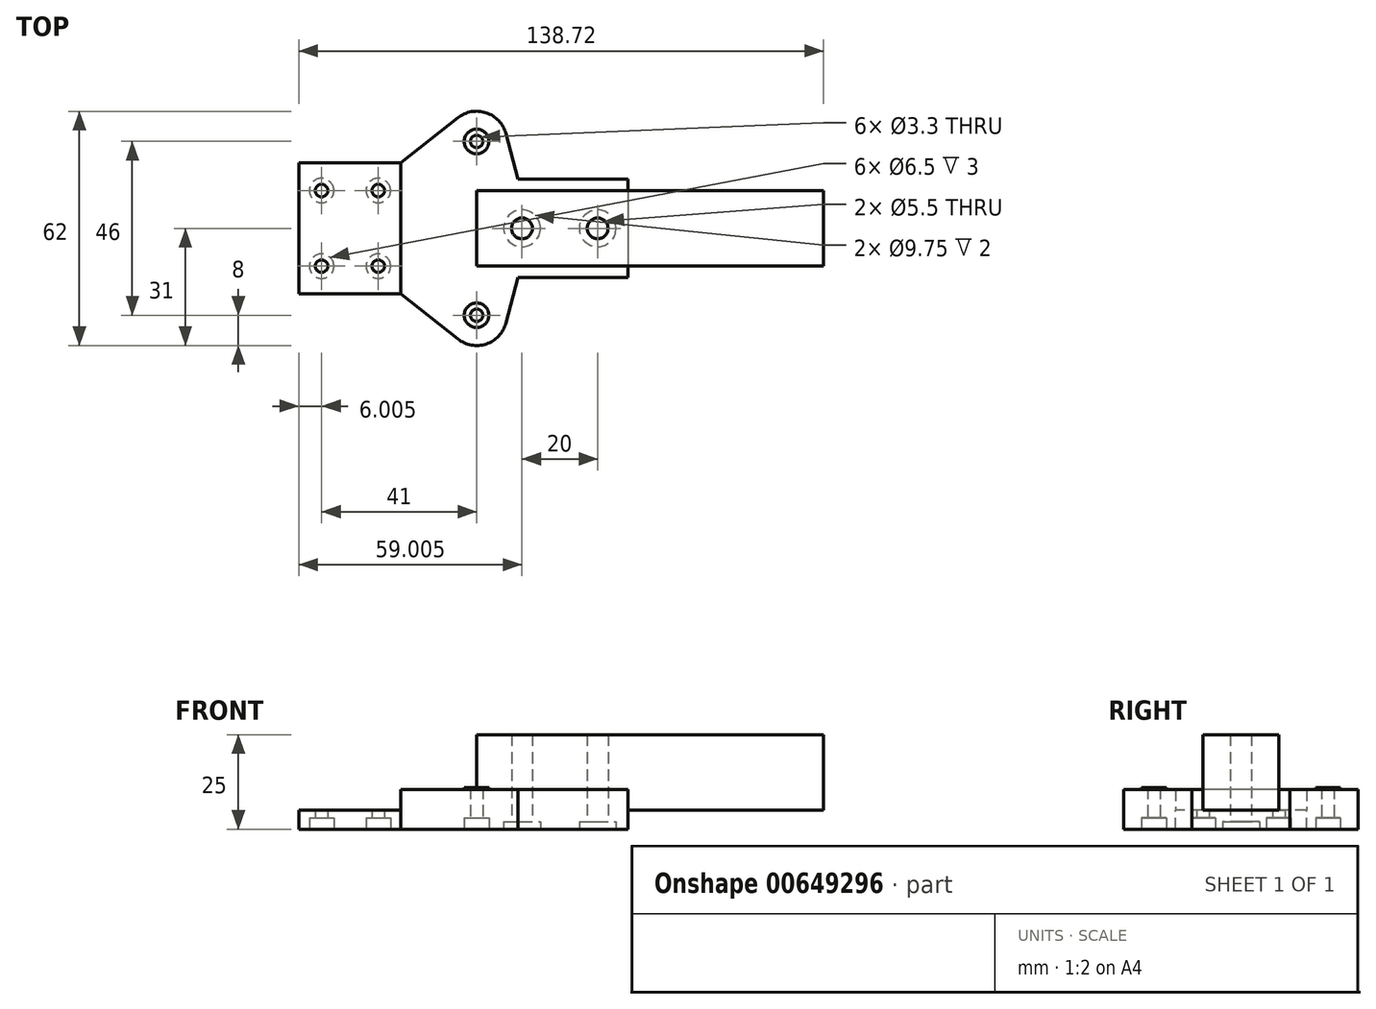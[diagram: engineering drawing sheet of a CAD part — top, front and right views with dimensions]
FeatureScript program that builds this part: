
annotation { "Feature Type Name" : "Feature", "Feature Type Description" : "" }
export const myFeature = defineFeature(function(context is Context, id is Id, definition is map)
    precondition{}
    {
        {
            var Q0;
            Q0=qCreatedBy(makeId("Top.planeOp"),FACE);
            var sketch = newSketch(context, id + "F0", { "sketchPlane" : qUnion([Q0])});
            skLineSegment(sketch, "E0.bottom", {"start": v(-72.66, 17.35) * mm, "end": v(-45.66, 17.35) * mm});
            skLineSegment(sketch, "E0.top", {"start": v(-72.66, -17.35) * mm, "end": v(-45.66, -17.35) * mm});
            skLineSegment(sketch, "E0.left", {"start": v(-72.66, 17.35) * mm, "end": v(-72.66, -17.35) * mm});
            skLineSegment(sketch, "E0.right", {"start": v(-45.66, 17.35) * mm, "end": v(-45.66, -17.35) * mm});
            skCircle(sketch, "E1", {"center": v(-25.66, 23) * mm, "radius": 8 * mm});
            skCircle(sketch, "E2", {"center": v(-25.66, -23) * mm, "radius": 8 * mm});
            skLineSegment(sketch, "E3.bottom", {"start": v(66.06, 10) * mm, "end": v(-25.66, 10) * mm});
            skLineSegment(sketch, "E3.top", {"start": v(66.06, -10) * mm, "end": v(-25.66, -10) * mm});
            skLineSegment(sketch, "E3.left", {"start": v(66.06, 10) * mm, "end": v(66.06, -10) * mm});
            skLineSegment(sketch, "E3.right", {"start": v(-25.66, 10) * mm, "end": v(-25.66, -10) * mm});
            skLineSegment(sketch, "E4", {"start": v(-45.66, 17.35) * mm, "end": v(-30.63, 29.27) * mm});
            skLineSegment(sketch, "E5", {"start": v(-45.66, -17.35) * mm, "end": v(-30.63, -29.27) * mm});
            skLineSegment(sketch, "E6", {"start": v(-13.89, -10) * mm, "end": v(-17.93, -25.07) * mm});
            skLineSegment(sketch, "E7", {"start": v(-13.89, 10) * mm, "end": v(-17.93, 25.07) * mm});
            skLineSegment(sketch, "E8", {"start": v(-14.7, 13) * mm, "end": v(14.34, 13) * mm});
            skLineSegment(sketch, "E9", {"start": v(14.34, 13) * mm, "end": v(14.34, -13) * mm});
            skLineSegment(sketch, "E10", {"start": v(14.34, -13) * mm, "end": v(-14.7, -13) * mm});
            skPoint(sketch, "E11.endSnap0", {"position": v(-38.14, 23.3) * mm});
            skSolve(sketch);
        }
        {
            var Q0;
            Q0=makeQuery(id+"F0.imprint","IMPRINT",FACE,{"disambiguationData":[TD([[makeQuery(id+"F0.imprint","IMPRINT",EDGE,{"derivedFrom":sQuery(id+"F0.wireOp",EDGE,"E0.bottom")}),-1.0]])]});
            var Q1;
            Q1=makeQuery(id+"F0.imprint","IMPRINT",FACE,{"disambiguationData":[TD([[makeQuery(id+"F0.imprint","IMPRINT",EDGE,{"derivedFrom":sQuery(id+"F0.wireOp",EDGE,"E0.right")}),1.0]])]});
            var Q2;
            {var subQ0=sQuery(id+"F0.wireOp",EDGE,"E1");var subQ1=makeQuery(id+"F0.imprint","INTERSECT",VERTEX,{"derivedFrom":[subQ0,sQuery(id+"F0.wireOp",EDGE,"E4")]});Q2=makeQuery(id+"F0.imprint","IMPRINT",FACE,{"disambiguationData":[TD([[makeQuery(id+"F0.imprint","IMPRINT",EDGE,{"disambiguationData":[TD([[subQ1,1.0]])],"derivedFrom":subQ0}),1.0]])]});}
            var Q3;
            {var subQ0=sQuery(id+"F0.wireOp",EDGE,"E2");var subQ1=makeQuery(id+"F0.imprint","INTERSECT",VERTEX,{"derivedFrom":[subQ0,sQuery(id+"F0.wireOp",EDGE,"E5")]});Q3=makeQuery(id+"F0.imprint","IMPRINT",FACE,{"disambiguationData":[TD([[makeQuery(id+"F0.imprint","IMPRINT",EDGE,{"disambiguationData":[TD([[subQ1,-1.0]])],"derivedFrom":subQ0}),1.0]])]});}
            var Q4;
            {var subQ5=sQuery(id+"F0.wireOp",EDGE,"E10");Q4=makeQuery(id+"F0.imprint","IMPRINT",FACE,{"disambiguationData":[TD([[makeQuery(id+"F0.imprint","IMPRINT",EDGE,{"derivedFrom":subQ5}),-1.0]])]});}
            var Q5;
            {var subQ5=sQuery(id+"F0.wireOp",EDGE,"E8");Q5=makeQuery(id+"F0.imprint","IMPRINT",FACE,{"disambiguationData":[TD([[makeQuery(id+"F0.imprint","IMPRINT",EDGE,{"derivedFrom":subQ5}),-1.0]])]});}
            var Q6;
            {var subQ0=sQuery(id+"F0.wireOp",EDGE,"E3.right");Q6=makeQuery(id+"F0.imprint","IMPRINT",FACE,{"disambiguationData":[TD([[makeQuery(id+"F0.imprint","IMPRINT",EDGE,{"derivedFrom":subQ0}),1.0]])]});}
            var Q7;
            {var subQ0=sQuery(id+"F0.wireOp",EDGE,"E3.right");Q7=makeQuery(id+"F0.imprint","IMPRINT",FACE,{"disambiguationData":[TD([[makeQuery(id+"F0.imprint","IMPRINT",EDGE,{"derivedFrom":subQ0}),-1.0]])]});}
            extrude(context, id + "F1", {"entities" : qUnion([Q0, Q1, Q2, Q3, Q4, Q5, Q6, Q7]), "oppositeDirection" : true, "depth" : 5 * mm, "offsetDistance" : 25 * mm});
        }
        {
            var Q0;
            {var subQ0=sQuery(id+"F0.wireOp",EDGE,"E3.left");Q0=makeQuery(id+"F0.imprint","IMPRINT",FACE,{"disambiguationData":[TD([[makeQuery(id+"F0.imprint","IMPRINT",EDGE,{"derivedFrom":subQ0}),-1.0]])]});}
            var Q1;
            {var subQ0=sQuery(id+"F0.wireOp",EDGE,"E3.right");Q1=makeQuery(id+"F0.imprint","IMPRINT",FACE,{"disambiguationData":[TD([[makeQuery(id+"F0.imprint","IMPRINT",EDGE,{"derivedFrom":subQ0}),1.0]])]});}
            extrude(context, id + "F2", {"entities" : qUnion([Q0, Q1]), "depth" : 20 * mm, "offsetDistance" : 25 * mm});
        }
        {
            var Q0;
            {var subQ0=sQuery(id+"F0.wireOp",EDGE,"E2");var subQ1=makeQuery(id+"F0.imprint","INTERSECT",VERTEX,{"derivedFrom":[subQ0,sQuery(id+"F0.wireOp",EDGE,"E5")]});Q0=makeQuery(id+"F0.imprint","IMPRINT",FACE,{"disambiguationData":[TD([[makeQuery(id+"F0.imprint","IMPRINT",EDGE,{"disambiguationData":[TD([[subQ1,-1.0]])],"derivedFrom":subQ0}),1.0]])]});}
            var Q1;
            {var subQ0=sQuery(id+"F0.wireOp",EDGE,"E1");var subQ1=makeQuery(id+"F0.imprint","INTERSECT",VERTEX,{"derivedFrom":[subQ0,sQuery(id+"F0.wireOp",EDGE,"E4")]});Q1=makeQuery(id+"F0.imprint","IMPRINT",FACE,{"disambiguationData":[TD([[makeQuery(id+"F0.imprint","IMPRINT",EDGE,{"disambiguationData":[TD([[subQ1,1.0]])],"derivedFrom":subQ0}),1.0]])]});}
            var Q2;
            Q2=makeQuery(id+"F0.imprint","IMPRINT",FACE,{"disambiguationData":[TD([[makeQuery(id+"F0.imprint","IMPRINT",EDGE,{"derivedFrom":sQuery(id+"F0.wireOp",EDGE,"E0.right")}),1.0]])]});
            var Q3;
            {var subQ5=sQuery(id+"F0.wireOp",EDGE,"E8");Q3=makeQuery(id+"F0.imprint","IMPRINT",FACE,{"disambiguationData":[TD([[makeQuery(id+"F0.imprint","IMPRINT",EDGE,{"derivedFrom":subQ5}),-1.0]])]});}
            var Q4;
            {var subQ5=sQuery(id+"F0.wireOp",EDGE,"E10");Q4=makeQuery(id+"F0.imprint","IMPRINT",FACE,{"disambiguationData":[TD([[makeQuery(id+"F0.imprint","IMPRINT",EDGE,{"derivedFrom":subQ5}),-1.0]])]});}
            var Q5;
            {var subQ0=sQuery(id+"F0.wireOp",EDGE,"E3.right");Q5=makeQuery(id+"F0.imprint","IMPRINT",FACE,{"disambiguationData":[TD([[makeQuery(id+"F0.imprint","IMPRINT",EDGE,{"derivedFrom":subQ0}),-1.0]])]});}
            extrude(context, id + "F3", {"entities" : qUnion([Q0, Q1, Q2, Q3, Q4, Q5]), "operationType" : NewBodyOperationType.ADD, "depth" : ((20 - 9) / 2) * mm, "offsetDistance" : 25 * mm});
        }
        {
            var Q0;
            Q0=makeQuery(id+"F1.opExtrude","CAP_FACE",FACE,{"disambiguationData":[OSD([sQuery(id+"F0.wireOp",EDGE,"E0.bottom"),sQuery(id+"F0.wireOp",EDGE,"E0.top"),sQuery(id+"F0.wireOp",EDGE,"E0.left"),sQuery(id+"F0.wireOp",EDGE,"E1"),sQuery(id+"F0.wireOp",EDGE,"E2"),sQuery(id+"F0.wireOp",EDGE,"E4"),sQuery(id+"F0.wireOp",EDGE,"E5"),sQuery(id+"F0.wireOp",EDGE,"E6"),sQuery(id+"F0.wireOp",EDGE,"E7"),sQuery(id+"F0.wireOp",EDGE,"E8"),sQuery(id+"F0.wireOp",EDGE,"E9"),sQuery(id+"F0.wireOp",EDGE,"E10")])],"isStart":false});
            var sketch = newSketch(context, id + "F4", { "sketchPlane" : qUnion([Q0])});
            skPoint(sketch, "E12", {"position": v(-25.66, 23) * mm});
            skPoint(sketch, "E13", {"position": v(-25.66, -23) * mm});
            skSolve(sketch);
        }
        {
            var Q0;
            Q0=sQuery(id+"F4.wireOp",VERTEX,"E12");
            var Q1;
            Q1=sQuery(id+"F4.wireOp",VERTEX,"E13");
            var Q2;
            Q2=makeQuery(id+"F1.opExtrude","SWEPT_BODY",BODY,{"disambiguationData":[OSD([sQuery(id+"F0.wireOp",EDGE,"E0.bottom"),sQuery(id+"F0.wireOp",EDGE,"E0.top"),sQuery(id+"F0.wireOp",EDGE,"E0.left"),sQuery(id+"F0.wireOp",EDGE,"E1"),sQuery(id+"F0.wireOp",EDGE,"E2"),sQuery(id+"F0.wireOp",EDGE,"E4"),sQuery(id+"F0.wireOp",EDGE,"E5"),sQuery(id+"F0.wireOp",EDGE,"E6"),sQuery(id+"F0.wireOp",EDGE,"E7"),sQuery(id+"F0.wireOp",EDGE,"E8"),sQuery(id+"F0.wireOp",EDGE,"E9"),sQuery(id+"F0.wireOp",EDGE,"E10")])]});
            hole(context, id + "F5", {"style" : HoleStyle.C_BORE, "endStyle" : HoleEndStyle.THROUGH, "standardTappedOrClearance" : lookupTablePath({ "standard" : "ISO", "fit" : "Normal", "size" : "M3", "type" : "Clearance" }), "standardBlindInLast" : lookupTablePath({ "fit" : "Standard", "standard" : "ISO", "size" : "M3", "type" : "Clearance" }), "holeDiameter" : 3.3 * mm, "cBoreDiameter" : 6.5 * mm, "cBoreDepth" : 3 * mm, "majorDiameter" : 5 * mm, "isTappedThrough" : true, "tappedDepth" : 15 * mm, "tapClearance" : 0, "startFromSketch" : true, "locations" : qUnion([Q0, Q1]), "scope" : qUnion([Q2])});
        }
        {
            var Q0;
            Q0=makeQuery(id+"F1.opExtrude","CAP_FACE",FACE,{"disambiguationData":[OSD([sQuery(id+"F0.wireOp",EDGE,"E0.bottom"),sQuery(id+"F0.wireOp",EDGE,"E0.top"),sQuery(id+"F0.wireOp",EDGE,"E0.left"),sQuery(id+"F0.wireOp",EDGE,"E1"),sQuery(id+"F0.wireOp",EDGE,"E2"),sQuery(id+"F0.wireOp",EDGE,"E4"),sQuery(id+"F0.wireOp",EDGE,"E5"),sQuery(id+"F0.wireOp",EDGE,"E6"),sQuery(id+"F0.wireOp",EDGE,"E7"),sQuery(id+"F0.wireOp",EDGE,"E8"),sQuery(id+"F0.wireOp",EDGE,"E9"),sQuery(id+"F0.wireOp",EDGE,"E10")])],"isStart":false});
            var sketch = newSketch(context, id + "F6", { "sketchPlane" : qUnion([Q0])});
            skPoint(sketch, "E14", {"position": v(-66.66, 10) * mm});
            skPoint(sketch, "E15", {"position": v(-66.66, -10) * mm});
            skPoint(sketch, "E16", {"position": v(-51.66, -10) * mm});
            skPoint(sketch, "E17", {"position": v(-51.66, 10) * mm});
            skSolve(sketch);
        }
        {
            var Q0;
            Q0=sQuery(id+"F6.wireOp",VERTEX,"E14");
            var Q1;
            Q1=sQuery(id+"F6.wireOp",VERTEX,"E15");
            var Q2;
            Q2=sQuery(id+"F6.wireOp",VERTEX,"E16");
            var Q3;
            Q3=sQuery(id+"F6.wireOp",VERTEX,"E17");
            var Q4;
            Q4=makeQuery(id+"F1.opExtrude","SWEPT_BODY",BODY,{"disambiguationData":[OSD([sQuery(id+"F0.wireOp",EDGE,"E0.bottom"),sQuery(id+"F0.wireOp",EDGE,"E0.top"),sQuery(id+"F0.wireOp",EDGE,"E0.left"),sQuery(id+"F0.wireOp",EDGE,"E1"),sQuery(id+"F0.wireOp",EDGE,"E2"),sQuery(id+"F0.wireOp",EDGE,"E4"),sQuery(id+"F0.wireOp",EDGE,"E5"),sQuery(id+"F0.wireOp",EDGE,"E6"),sQuery(id+"F0.wireOp",EDGE,"E7"),sQuery(id+"F0.wireOp",EDGE,"E8"),sQuery(id+"F0.wireOp",EDGE,"E9"),sQuery(id+"F0.wireOp",EDGE,"E10")])]});
            hole(context, id + "F7", {"style" : HoleStyle.C_BORE, "endStyle" : HoleEndStyle.THROUGH, "standardTappedOrClearance" : lookupTablePath({ "standard" : "ISO", "fit" : "Normal", "size" : "M3", "type" : "Clearance" }), "standardBlindInLast" : lookupTablePath({ "fit" : "Standard", "standard" : "ISO", "size" : "M3", "type" : "Clearance" }), "holeDiameter" : 3.3 * mm, "cBoreDiameter" : 6.5 * mm, "cBoreDepth" : 3 * mm, "majorDiameter" : 5 * mm, "isTappedThrough" : true, "tappedDepth" : 15 * mm, "tapClearance" : 0, "startFromSketch" : true, "locations" : qUnion([Q0, Q1, Q2, Q3]), "scope" : qUnion([Q4])});
        }
        {
            var Q0;
            Q0=makeQuery(id+"F1.opExtrude","CAP_FACE",FACE,{"disambiguationData":[OSD([sQuery(id+"F0.wireOp",EDGE,"E0.bottom"),sQuery(id+"F0.wireOp",EDGE,"E0.top"),sQuery(id+"F0.wireOp",EDGE,"E0.left"),sQuery(id+"F0.wireOp",EDGE,"E1"),sQuery(id+"F0.wireOp",EDGE,"E2"),sQuery(id+"F0.wireOp",EDGE,"E4"),sQuery(id+"F0.wireOp",EDGE,"E5"),sQuery(id+"F0.wireOp",EDGE,"E6"),sQuery(id+"F0.wireOp",EDGE,"E7"),sQuery(id+"F0.wireOp",EDGE,"E8"),sQuery(id+"F0.wireOp",EDGE,"E9"),sQuery(id+"F0.wireOp",EDGE,"E10")])],"isStart":false});
            var sketch = newSketch(context, id + "F8", { "sketchPlane" : qUnion([Q0])});
            skPoint(sketch, "E18", {"position": v(6.34, 0) * mm});
            skPoint(sketch, "E19", {"position": v(-13.66, 0) * mm});
            skSolve(sketch);
        }
        {
            var Q0;
            Q0=sQuery(id+"F8.wireOp",VERTEX,"E19");
            var Q1;
            Q1=sQuery(id+"F8.wireOp",VERTEX,"E18");
            var Q2;
            Q2=makeQuery(id+"F1.opExtrude","SWEPT_BODY",BODY,{"disambiguationData":[OSD([sQuery(id+"F0.wireOp",EDGE,"E0.bottom"),sQuery(id+"F0.wireOp",EDGE,"E0.top"),sQuery(id+"F0.wireOp",EDGE,"E0.left"),sQuery(id+"F0.wireOp",EDGE,"E1"),sQuery(id+"F0.wireOp",EDGE,"E2"),sQuery(id+"F0.wireOp",EDGE,"E4"),sQuery(id+"F0.wireOp",EDGE,"E5"),sQuery(id+"F0.wireOp",EDGE,"E6"),sQuery(id+"F0.wireOp",EDGE,"E7"),sQuery(id+"F0.wireOp",EDGE,"E8"),sQuery(id+"F0.wireOp",EDGE,"E9"),sQuery(id+"F0.wireOp",EDGE,"E10")])]});
            var Q3;
            Q3=makeQuery(id+"F2.opExtrude","SWEPT_BODY",BODY,{"disambiguationData":[OSD([sQuery(id+"F0.wireOp",EDGE,"E3.bottom"),sQuery(id+"F0.wireOp",EDGE,"E3.top"),sQuery(id+"F0.wireOp",EDGE,"E3.left"),sQuery(id+"F0.wireOp",EDGE,"E3.right")])]});
            hole(context, id + "F9", {"style" : HoleStyle.C_BORE, "endStyle" : HoleEndStyle.THROUGH, "holeDiameter" : 5.5 * mm, "cBoreDiameter" : 9.75 * mm, "cBoreDepth" : 2 * mm, "majorDiameter" : 5 * mm, "isTappedThrough" : true, "tappedDepth" : 15 * mm, "tapClearance" : 0, "startFromSketch" : true, "locations" : qUnion([Q0, Q1]), "scope" : qUnion([Q2, Q3])});
        }
        {
            var Q0;
            Q0=makeQuery(id+"F3.opExtrude","CAP_FACE",FACE,{"disambiguationData":[OSD([sQuery(id+"F0.wireOp",EDGE,"E0.right"),sQuery(id+"F0.wireOp",EDGE,"E1"),sQuery(id+"F0.wireOp",EDGE,"E2"),sQuery(id+"F0.wireOp",EDGE,"E3.bottom"),sQuery(id+"F0.wireOp",EDGE,"E3.top"),sQuery(id+"F0.wireOp",EDGE,"E3.right"),sQuery(id+"F0.wireOp",EDGE,"E4"),sQuery(id+"F0.wireOp",EDGE,"E5"),sQuery(id+"F0.wireOp",EDGE,"E6"),sQuery(id+"F0.wireOp",EDGE,"E7"),sQuery(id+"F0.wireOp",EDGE,"E8"),sQuery(id+"F0.wireOp",EDGE,"E9"),sQuery(id+"F0.wireOp",EDGE,"E10")])],"isStart":false});
            var sketch = newSketch(context, id + "F10", { "sketchPlane" : qUnion([Q0])});
            skCircle(sketch, "E20", {"center": v(-25.66, 23) * mm, "radius": 3.25 * mm});
            skCircle(sketch, "E21", {"center": v(-25.66, -23) * mm, "radius": 3.25 * mm});
            skSolve(sketch);
        }
        {
            var Q0;
            Q0=makeQuery(id+"F10.imprint","IMPRINT",FACE,{"disambiguationData":[TD([[makeQuery(id+"F10.imprint","IMPRINT",EDGE,{"derivedFrom":sQuery(id+"F10.wireOp",EDGE,"E21")}),1.0]])]});
            var Q1;
            Q1=makeQuery(id+"F10.imprint","IMPRINT",FACE,{"disambiguationData":[TD([[makeQuery(id+"F10.imprint","IMPRINT",EDGE,{"derivedFrom":sQuery(id+"F10.wireOp",EDGE,"E20")}),1.0]])]});
            extrude(context, id + "F11", {"entities" : qUnion([Q0, Q1]), "operationType" : NewBodyOperationType.ADD, "depth" : .5 * mm, "offsetDistance" : 25 * mm});
        }
    });
